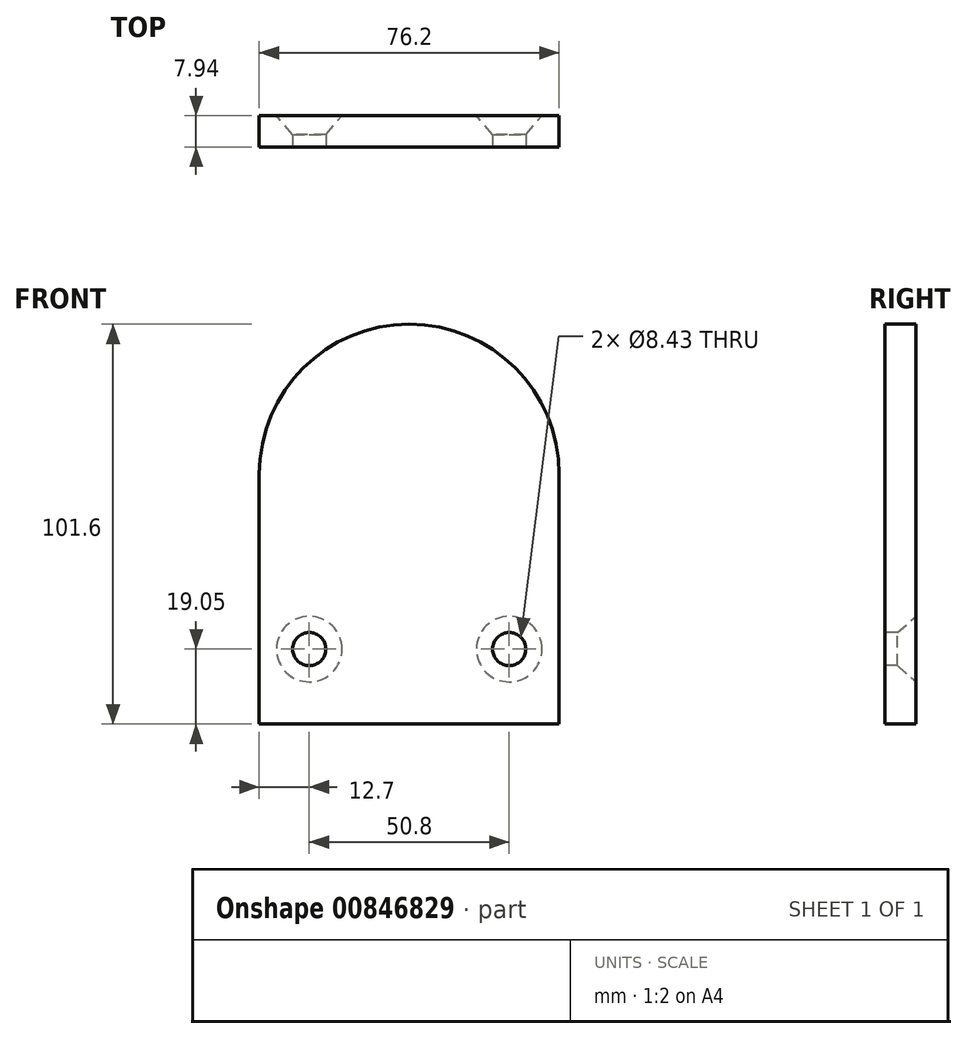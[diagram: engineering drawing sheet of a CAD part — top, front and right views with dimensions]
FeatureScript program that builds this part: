
annotation { "Feature Type Name" : "Feature", "Feature Type Description" : "" }
export const myFeature = defineFeature(function(context is Context, id is Id, definition is map)
    precondition{}
    {
        {
            var Q0;
            Q0=qCreatedBy(makeId("Front.planeOp"),FACE);
            var sketch = newSketch(context, id + "F0", { "sketchPlane" : qUnion([Q0])});
            skCircle(sketch, "E0", {"center": v(0, 0) * mm, "radius": 25.78 * mm, "construction": true});
            skArc(sketch, "E1", {"start": v(38.1, 0) * mm, "mid": v(0, 38.1) * mm, "end": v(-38.1, 0) * mm});
            skLineSegment(sketch, "E2.top", {"start": v(-38.1, -63.5) * mm, "end": v(38.1, -63.5) * mm});
            skLineSegment(sketch, "E2.left", {"start": v(-38.1, 0) * mm, "end": v(-38.1, -63.5) * mm});
            skLineSegment(sketch, "E2.right", {"start": v(38.1, 0) * mm, "end": v(38.1, -63.5) * mm});
            skLineSegment(sketch, "E3", {"start": v(-25.4, -44.45) * mm, "end": v(25.4, -44.45) * mm, "construction": true});
            skLineSegment(sketch, "E4", {"start": v(0, 0) * mm, "end": v(0, -44.45) * mm, "construction": true});
            skCircle(sketch, "E5", {"center": v(-25.4, -44.45) * mm, "radius": 4.32 * mm, "construction": true});
            skCircle(sketch, "E6", {"center": v(25.4, -44.45) * mm, "radius": 4.32 * mm, "construction": true});
            skSolve(sketch);
        }
        {
            var Q0;
            Q0 = qSketchRegion(id + "F0", true);
            extrude(context, id + "F1", {"entities" : qUnion([Q0]), "depth" : 7.94 * mm, "offsetDistance" : 25.4 * mm});
        }
        {
            var Q0;
            Q0=sQuery(id+"F0.wireOp",VERTEX,"E5.center");
            var Q1;
            Q1=sQuery(id+"F0.wireOp",VERTEX,"E6.center");
            var Q2;
            Q2=makeQuery(id+"F1.opExtrude","SWEPT_BODY",BODY,{"disambiguationData":[OSD([sQuery(id+"F0.wireOp",EDGE,"E1"),sQuery(id+"F0.wireOp",EDGE,"E2.top"),sQuery(id+"F0.wireOp",EDGE,"E2.left"),sQuery(id+"F0.wireOp",EDGE,"E2.right")])]});
            hole(context, id + "F2", {"style" : HoleStyle.C_SINK, "endStyle" : HoleEndStyle.THROUGH, "oppositeDirection" : true, "standardTappedOrClearance" : lookupTablePath({ "fit" : "Free", "standard" : "ANSI", "size" : "5/16", "type" : "Clearance" }), "standardBlindInLast" : lookupTablePath({ "fit" : "Free", "standard" : "ANSI", "engagement" : "75%", "pitch" : "18 tpi", "size" : "5/16", "type" : "Clearance & tapped" }), "holeDiameter" : 8.43 * mm, "cSinkDiameter" : 16.66 * mm, "cSinkAngle" : 82 * degree, "majorDiameter" : 6.35 * mm, "tappedDepth" : 9.52 * mm, "tapClearance" : 3, "locations" : qUnion([Q0, Q1]), "scope" : qUnion([Q2]), "startStyle" : HoleStartStyle.SKETCH});
        }
    });
